# Revit family: QF_Vollrath_MB36
name_source: partatom
category: Specialty Equipment
revit_build: Autodesk Revit 2018 (Build: 20190510_1515(x64)
units: mm (PartAtom-declared; Revit-internal decimal feet)

## family parameters
Always vertical = Yes
Cut with Voids When Loaded = Yes
Part Type = Normal
Room Calculation Point = No
Round Connector Dimension = Use Diameter
Shared = No
Work Plane-Based = No

## types (3) — shared parameters
Description = Mobile Breath Guard
Furnished By = KEC
Height = 16 1/2"
Height Constraint = 16 1/2"
Include In Foodservice Schedule = Yes
Installed By = KEC
Manufacturer = Vollrath
TM Utilties = 0
zero-valued in all types: Cost, Weight in Pounds

## per-type parameters (varying)
| type | Curved Glass | Flat Glass | Legs | Mounted |
| MB36 | Yes | No | Yes | No |
| MB36FLAT | No | Yes | Yes | No |
| MB36MOUNT | No | Yes | No | Yes |

note: column(s) folded — value = type name in every type: Model

## geometry (parser evidence)
native form markers: Sweep x8
no freeform markers — native parametric forms only
